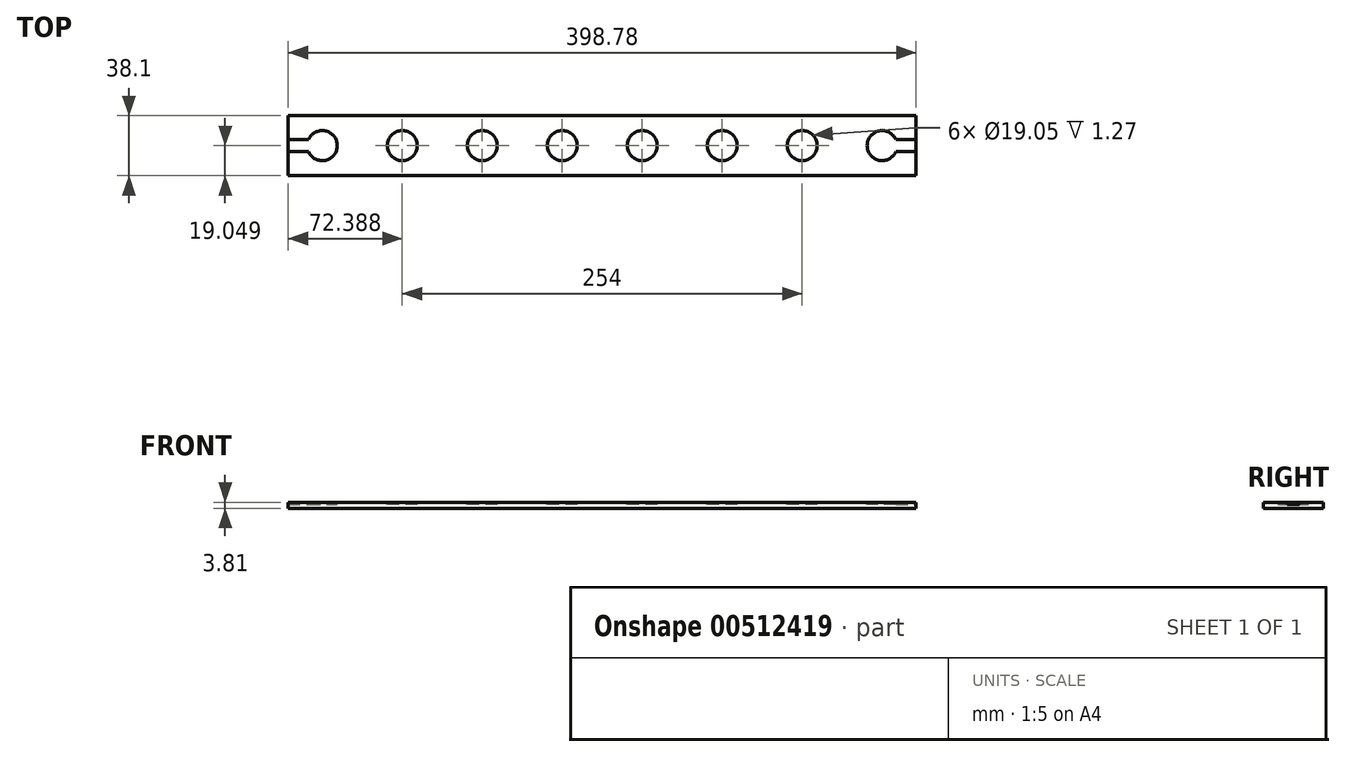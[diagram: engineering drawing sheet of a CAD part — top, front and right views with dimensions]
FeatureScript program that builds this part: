
annotation { "Feature Type Name" : "Feature", "Feature Type Description" : "" }
export const myFeature = defineFeature(function(context is Context, id is Id, definition is map)
    precondition{}
    {
        {
            var Q0;
            Q0=qCreatedBy(makeId("Top.planeOp"),FACE);
            var sketch = newSketch(context, id + "F0", { "sketchPlane" : qUnion([Q0])});
            skLineSegment(sketch, "E0.bottom", {"start": v(-114.3, 40.5) * mm, "end": v(284.49, 40.5) * mm});
            skLineSegment(sketch, "E0.top", {"start": v(-114.3, 2.4) * mm, "end": v(284.49, 2.4) * mm});
            skLineSegment(sketch, "E0.left", {"start": v(-114.3, 40.5) * mm, "end": v(-114.3, 2.4) * mm});
            skLineSegment(sketch, "E0.right", {"start": v(284.49, 40.5) * mm, "end": v(284.49, 2.4) * mm});
            skSolve(sketch);
        }
        {
            var Q0;
            Q0=makeQuery(id+"F0.imprint","IMPRINT",FACE,{"disambiguationData":[TD([[makeQuery(id+"F0.imprint","IMPRINT",EDGE,{"derivedFrom":sQuery(id+"F0.wireOp",EDGE,"E0.bottom")}),-1.0]])]});
            extrude(context, id + "F1", {"entities" : qUnion([Q0]), "depth" : 3.8 * mm});
        }
        {
            var Q0;
            Q0=makeQuery(id+"F1.opExtrude","CAP_FACE",FACE,{"disambiguationData":[OSD([sQuery(id+"F0.wireOp",EDGE,"E0.bottom"),sQuery(id+"F0.wireOp",EDGE,"E0.top"),sQuery(id+"F0.wireOp",EDGE,"E0.left"),sQuery(id+"F0.wireOp",EDGE,"E0.right")])],"isStart":false});
            var sketch = newSketch(context, id + "F2", { "sketchPlane" : qUnion([Q0])});
            skCircle(sketch, "E1", {"center": v(-92.7, 21.46) * mm, "radius": 9.52 * mm});
            skCircle(sketch, "E2.1.0.0", {"center": v(-41.9, 21.46) * mm, "radius": 9.52 * mm});
            skCircle(sketch, "E2.2.0.0", {"center": v(8.9, 21.46) * mm, "radius": 9.52 * mm});
            skCircle(sketch, "E2.3.0.0", {"center": v(59.7, 21.46) * mm, "radius": 9.52 * mm});
            skCircle(sketch, "E2.4.0.0", {"center": v(110.5, 21.46) * mm, "radius": 9.52 * mm});
            skCircle(sketch, "E2.5.0.0", {"center": v(161.3, 21.46) * mm, "radius": 9.52 * mm});
            skCircle(sketch, "E2.6.0.0", {"center": v(212.1, 21.46) * mm, "radius": 9.52 * mm});
            skCircle(sketch, "E2.7.0.0", {"center": v(262.9, 21.46) * mm, "radius": 9.52 * mm});
            skLineSegment(sketch, "E2.direction1", {"start": v(-92.7, 21.46) * mm, "end": v(-41.9, 21.46) * mm, "construction": true});
            skSolve(sketch);
        }
        {
            var Q0;
            Q0=makeQuery(id+"F2.imprint","IMPRINT",FACE,{"disambiguationData":[TD([[makeQuery(id+"F2.imprint","IMPRINT",EDGE,{"derivedFrom":sQuery(id+"F2.wireOp",EDGE,"E1")}),1.0]])]});
            var Q1;
            Q1=makeQuery(id+"F2.imprint","IMPRINT",FACE,{"disambiguationData":[TD([[makeQuery(id+"F2.imprint","IMPRINT",EDGE,{"derivedFrom":sQuery(id+"F2.wireOp",EDGE,"E2.1.0.0")}),1.0]])]});
            var Q2;
            Q2=makeQuery(id+"F2.imprint","IMPRINT",FACE,{"disambiguationData":[TD([[makeQuery(id+"F2.imprint","IMPRINT",EDGE,{"derivedFrom":sQuery(id+"F2.wireOp",EDGE,"E2.2.0.0")}),1.0]])]});
            var Q3;
            Q3=makeQuery(id+"F2.imprint","IMPRINT",FACE,{"disambiguationData":[TD([[makeQuery(id+"F2.imprint","IMPRINT",EDGE,{"derivedFrom":sQuery(id+"F2.wireOp",EDGE,"E2.3.0.0")}),1.0]])]});
            var Q4;
            Q4=makeQuery(id+"F2.imprint","IMPRINT",FACE,{"disambiguationData":[TD([[makeQuery(id+"F2.imprint","IMPRINT",EDGE,{"derivedFrom":sQuery(id+"F2.wireOp",EDGE,"E2.4.0.0")}),1.0]])]});
            var Q5;
            Q5=makeQuery(id+"F2.imprint","IMPRINT",FACE,{"disambiguationData":[TD([[makeQuery(id+"F2.imprint","IMPRINT",EDGE,{"derivedFrom":sQuery(id+"F2.wireOp",EDGE,"E2.5.0.0")}),1.0]])]});
            var Q6;
            Q6=makeQuery(id+"F2.imprint","IMPRINT",FACE,{"disambiguationData":[TD([[makeQuery(id+"F2.imprint","IMPRINT",EDGE,{"derivedFrom":sQuery(id+"F2.wireOp",EDGE,"E2.6.0.0")}),1.0]])]});
            var Q7;
            Q7=makeQuery(id+"F2.imprint","IMPRINT",FACE,{"disambiguationData":[TD([[makeQuery(id+"F2.imprint","IMPRINT",EDGE,{"derivedFrom":sQuery(id+"F2.wireOp",EDGE,"E2.7.0.0")}),1.0]])]});
            extrude(context, id + "F3", {"entities" : qUnion([Q0, Q1, Q2, Q3, Q4, Q5, Q6, Q7]), "operationType" : NewBodyOperationType.REMOVE, "oppositeDirection" : true, "depth" : 1.27 * mm});
        }
        {
            var Q0;
            Q0=makeQuery(id+"F1.opExtrude","CAP_FACE",FACE,{"disambiguationData":[OSD([sQuery(id+"F0.wireOp",EDGE,"E0.bottom"),sQuery(id+"F0.wireOp",EDGE,"E0.top"),sQuery(id+"F0.wireOp",EDGE,"E0.left"),sQuery(id+"F0.wireOp",EDGE,"E0.right")])],"isStart":false});
            var sketch = newSketch(context, id + "F4", { "sketchPlane" : qUnion([Q0])});
            skLineSegment(sketch, "E3.bottom", {"start": v(-114.3, 25.27) * mm, "end": v(284.49, 25.27) * mm});
            skLineSegment(sketch, "E3.top", {"start": v(-114.3, 17.65) * mm, "end": v(284.49, 17.65) * mm});
            skLineSegment(sketch, "E3.left", {"start": v(-114.3, 25.27) * mm, "end": v(-114.3, 17.65) * mm});
            skLineSegment(sketch, "E3.right", {"start": v(284.49, 25.27) * mm, "end": v(284.49, 17.65) * mm});
            skSolve(sketch);
        }
        {
            var Q0;
            {var subQ0=sQuery(id+"F4.wireOp",EDGE,"E3.bottom");var subQ1=makeQuery(id+"F3.boolean.opBoolean","COPY",EDGE,{"derivedFrom":makeQuery(id+"F3.opExtrude","CAP_EDGE",EDGE,{"disambiguationData":[OSD([sQuery(id+"F2.wireOp",EDGE,"E1")])],"isStart":true})});var subQ2=makeQuery(id+"F4.imprint","INTERSECT",VERTEX,{"disambiguationData":[OD(1.0)],"derivedFrom":[subQ1,subQ0]});Q0=makeQuery(id+"F4.imprint","IMPRINT",FACE,{"disambiguationData":[TD([[makeQuery(id+"F4.imprint","IMPRINT",EDGE,{"disambiguationData":[TD([[subQ2,-1.0]])],"derivedFrom":subQ0}),-1.0]])]});}
            var Q1;
            {var subQ0=sQuery(id+"F4.wireOp",EDGE,"E3.left");Q1=makeQuery(id+"F4.imprint","IMPRINT",FACE,{"disambiguationData":[TD([[makeQuery(id+"F4.imprint","IMPRINT",EDGE,{"derivedFrom":subQ0}),1.0]])]});}
            var Q2;
            {var subQ0=sQuery(id+"F4.wireOp",EDGE,"E3.bottom");var subQ1=makeQuery(id+"F3.boolean.opBoolean","COPY",EDGE,{"derivedFrom":makeQuery(id+"F3.opExtrude","CAP_EDGE",EDGE,{"disambiguationData":[OSD([sQuery(id+"F2.wireOp",EDGE,"E2.1.0.0")])],"isStart":true})});var subQ2=makeQuery(id+"F4.imprint","INTERSECT",VERTEX,{"disambiguationData":[OD(1.0)],"derivedFrom":[subQ1,subQ0]});Q2=makeQuery(id+"F4.imprint","IMPRINT",FACE,{"disambiguationData":[TD([[makeQuery(id+"F4.imprint","IMPRINT",EDGE,{"disambiguationData":[TD([[subQ2,-1.0]])],"derivedFrom":subQ0}),-1.0]])]});}
            var Q3;
            {var subQ0=sQuery(id+"F4.wireOp",EDGE,"E3.bottom");var subQ1=makeQuery(id+"F3.boolean.opBoolean","COPY",EDGE,{"derivedFrom":makeQuery(id+"F3.opExtrude","CAP_EDGE",EDGE,{"disambiguationData":[OSD([sQuery(id+"F2.wireOp",EDGE,"E2.2.0.0")])],"isStart":true})});var subQ2=makeQuery(id+"F4.imprint","INTERSECT",VERTEX,{"disambiguationData":[OD(1.0)],"derivedFrom":[subQ1,subQ0]});Q3=makeQuery(id+"F4.imprint","IMPRINT",FACE,{"disambiguationData":[TD([[makeQuery(id+"F4.imprint","IMPRINT",EDGE,{"disambiguationData":[TD([[subQ2,-1.0]])],"derivedFrom":subQ0}),-1.0]])]});}
            var Q4;
            {var subQ0=sQuery(id+"F4.wireOp",EDGE,"E3.bottom");var subQ1=makeQuery(id+"F3.boolean.opBoolean","COPY",EDGE,{"derivedFrom":makeQuery(id+"F3.opExtrude","CAP_EDGE",EDGE,{"disambiguationData":[OSD([sQuery(id+"F2.wireOp",EDGE,"E2.3.0.0")])],"isStart":true})});var subQ2=makeQuery(id+"F4.imprint","INTERSECT",VERTEX,{"disambiguationData":[OD(1.0)],"derivedFrom":[subQ1,subQ0]});Q4=makeQuery(id+"F4.imprint","IMPRINT",FACE,{"disambiguationData":[TD([[makeQuery(id+"F4.imprint","IMPRINT",EDGE,{"disambiguationData":[TD([[subQ2,-1.0]])],"derivedFrom":subQ0}),-1.0]])]});}
            var Q5;
            {var subQ0=sQuery(id+"F4.wireOp",EDGE,"E3.bottom");var subQ1=makeQuery(id+"F3.boolean.opBoolean","COPY",EDGE,{"derivedFrom":makeQuery(id+"F3.opExtrude","CAP_EDGE",EDGE,{"disambiguationData":[OSD([sQuery(id+"F2.wireOp",EDGE,"E2.4.0.0")])],"isStart":true})});var subQ2=makeQuery(id+"F4.imprint","INTERSECT",VERTEX,{"disambiguationData":[OD(1.0)],"derivedFrom":[subQ1,subQ0]});Q5=makeQuery(id+"F4.imprint","IMPRINT",FACE,{"disambiguationData":[TD([[makeQuery(id+"F4.imprint","IMPRINT",EDGE,{"disambiguationData":[TD([[subQ2,-1.0]])],"derivedFrom":subQ0}),-1.0]])]});}
            var Q6;
            {var subQ0=sQuery(id+"F4.wireOp",EDGE,"E3.bottom");var subQ1=makeQuery(id+"F3.boolean.opBoolean","COPY",EDGE,{"derivedFrom":makeQuery(id+"F3.opExtrude","CAP_EDGE",EDGE,{"disambiguationData":[OSD([sQuery(id+"F2.wireOp",EDGE,"E2.6.0.0")])],"isStart":true})});var subQ2=makeQuery(id+"F4.imprint","INTERSECT",VERTEX,{"disambiguationData":[OD(1.0)],"derivedFrom":[subQ1,subQ0]});Q6=makeQuery(id+"F4.imprint","IMPRINT",FACE,{"disambiguationData":[TD([[makeQuery(id+"F4.imprint","IMPRINT",EDGE,{"disambiguationData":[TD([[subQ2,-1.0]])],"derivedFrom":subQ0}),-1.0]])]});}
            var Q7;
            {var subQ0=sQuery(id+"F4.wireOp",EDGE,"E3.right");Q7=makeQuery(id+"F4.imprint","IMPRINT",FACE,{"disambiguationData":[TD([[makeQuery(id+"F4.imprint","IMPRINT",EDGE,{"derivedFrom":subQ0}),-1.0]])]});}
            var Q8;
            {var subQ0=sQuery(id+"F4.wireOp",EDGE,"E3.bottom");var subQ1=makeQuery(id+"F3.boolean.opBoolean","COPY",EDGE,{"derivedFrom":makeQuery(id+"F3.opExtrude","CAP_EDGE",EDGE,{"disambiguationData":[OSD([sQuery(id+"F2.wireOp",EDGE,"E2.5.0.0")])],"isStart":true})});var subQ2=makeQuery(id+"F4.imprint","INTERSECT",VERTEX,{"disambiguationData":[OD(1.0)],"derivedFrom":[subQ1,subQ0]});Q8=makeQuery(id+"F4.imprint","IMPRINT",FACE,{"disambiguationData":[TD([[makeQuery(id+"F4.imprint","IMPRINT",EDGE,{"disambiguationData":[TD([[subQ2,-1.0]])],"derivedFrom":subQ0}),-1.0]])]});}
            extrude(context, id + "F5", {"entities" : qUnion([Q0, Q1, Q2, Q3, Q4, Q5, Q6, Q7, Q8]), "operationType" : NewBodyOperationType.REMOVE, "oppositeDirection" : true, "depth" : 1.27 * mm});
        }
    });
